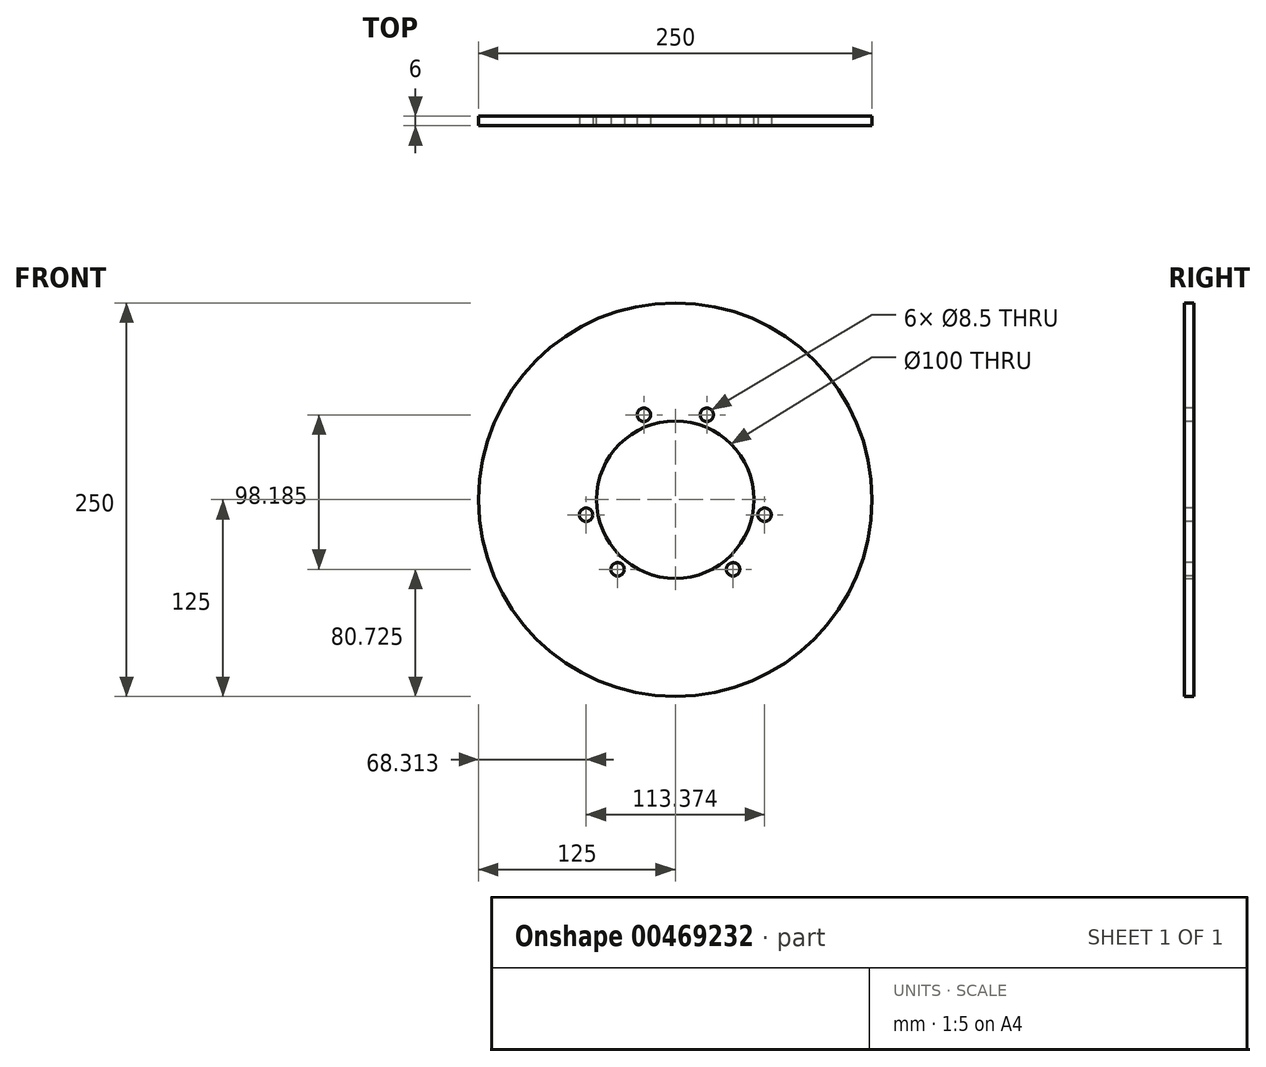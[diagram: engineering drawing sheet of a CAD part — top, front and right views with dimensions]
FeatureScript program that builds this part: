
annotation { "Feature Type Name" : "Feature", "Feature Type Description" : "" }
export const myFeature = defineFeature(function(context is Context, id is Id, definition is map)
    precondition{}
    {
        {
            var Q0;
            Q0=qCreatedBy(makeId("Front.planeOp"),FACE);
            var sketch = newSketch(context, id + "F0", { "sketchPlane" : qUnion([Q0])});
            skCircle(sketch, "E0", {"center": v(0, 0) * mm, "radius": 50 * mm});
            skCircle(sketch, "E1", {"center": v(0, 0) * mm, "radius": 125 * mm});
            skSolve(sketch);
        }
        {
            var Q0;
            Q0 = qSketchRegion(id + "F0", true);
            extrude(context, id + "F1", {"entities" : qUnion([Q0]), "endBound" : BoundingType.SYMMETRIC, "depth" : 6 * mm});
        }
        {
            var Q0;
            Q0=makeQuery(id+"F1.opExtrude","CAP_FACE",FACE,{"disambiguationData":[OSD([sQuery(id+"F0.wireOp",EDGE,"E0"),sQuery(id+"F0.wireOp",EDGE,"E1")])],"isStart":false});
            var sketch = newSketch(context, id + "F2", { "sketchPlane" : qUnion([Q0])});
            skPoint(sketch, "E2", {"position": v(-20, 53.9) * mm});
            skCircle(sketch, "E3", {"center": v(0, 0) * mm, "radius": 57.5 * mm, "construction": true});
            skLineSegment(sketch, "E4", {"start": v(0, 0) * mm, "end": v(0, 57.5) * mm, "construction": true});
            skPoint(sketch, "E5.MirrorP", {"position": v(20, 53.9) * mm});
            skPoint(sketch, "E6.1.0", {"position": v(-36.69, -44.28) * mm});
            skPoint(sketch, "E6.1.1", {"position": v(-56.69, -9.63) * mm});
            skPoint(sketch, "E6.2.0", {"position": v(56.69, -9.63) * mm});
            skPoint(sketch, "E6.2.1", {"position": v(36.69, -44.28) * mm});
            skSolve(sketch);
        }
        {
            var Q0;
            Q0=sQuery(id+"F2.wireOp",VERTEX,"E2");
            var Q1;
            Q1=sQuery(id+"F2.wireOp",VERTEX,"E5.MirrorP");
            var Q2;
            Q2=sQuery(id+"F2.wireOp",VERTEX,"E6.2.0");
            var Q3;
            Q3=sQuery(id+"F2.wireOp",VERTEX,"E6.2.1");
            var Q4;
            Q4=sQuery(id+"F2.wireOp",VERTEX,"E6.1.0");
            var Q5;
            Q5=sQuery(id+"F2.wireOp",VERTEX,"E6.1.1");
            var Q6;
            Q6=makeQuery(id+"F1.opExtrude","SWEPT_BODY",BODY,{"disambiguationData":[OSD([sQuery(id+"F0.wireOp",EDGE,"E0"),sQuery(id+"F0.wireOp",EDGE,"E1")])]});
            hole(context, id + "F3", {"style" : HoleStyle.SIMPLE, "endStyle" : HoleEndStyle.THROUGH, "holeDiameter" : 8.5 * mm, "isTappedThrough" : true, "tappedDepth" : 12 * mm, "tapClearance" : 3, "locations" : qUnion([Q0, Q1, Q2, Q3, Q4, Q5]), "scope" : qUnion([Q6])});
        }
    });
